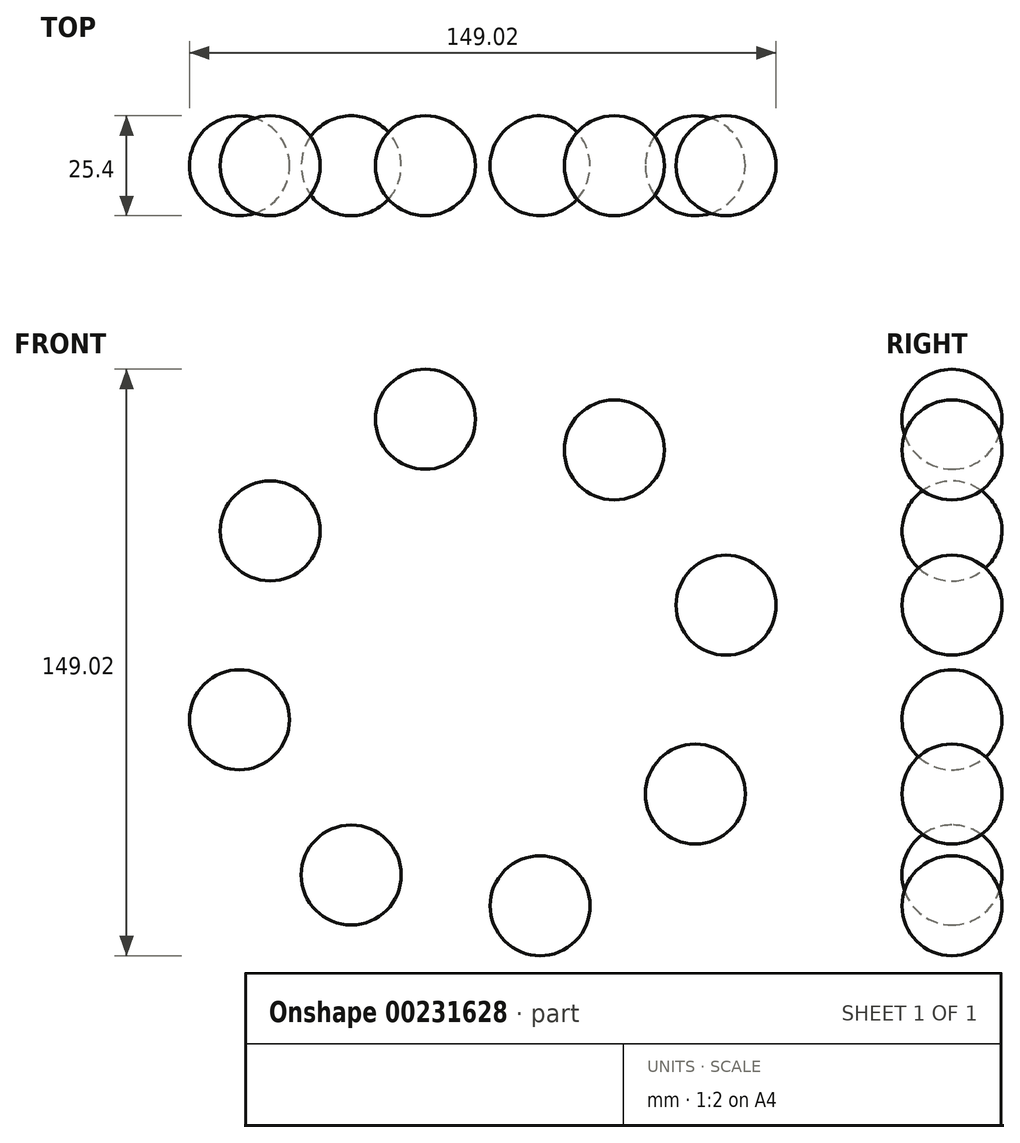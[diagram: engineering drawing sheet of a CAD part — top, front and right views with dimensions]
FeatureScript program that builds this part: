
annotation { "Feature Type Name" : "Feature", "Feature Type Description" : "" }
export const myFeature = defineFeature(function(context is Context, id is Id, definition is map)
    precondition{}
    {
        {
            var Q0;
            Q0=qCreatedBy(makeId("Front.planeOp"),FACE);
            var sketch = newSketch(context, id + "F2", { "sketchPlane" : qUnion([Q0])});
            skCircle(sketch, "E0", {"center": v(0, 0) * mm, "radius": 12.7 * mm});
            skLineSegment(sketch, "E1", {"start": v(0, 28.88) * mm, "end": v(0, -33.86) * mm});
            skCircle(sketch, "E2", {"center": v(33.41, 54) * mm, "radius": 63.5 * mm});
            skPoint(sketch, "E2.second.point", {"position": v(69.32, 106.37) * mm});
            skPoint(sketch, "E2.third.point", {"position": v(83.1, 93.54) * mm});
            skSolve(sketch);
        }
        {
            var Q0;
            {var subQ0=sQuery(id+"F2.wireOp",EDGE,"E1");var subQ1=sQuery(id+"F2.wireOp",EDGE,"E0");var subQ2=makeQuery(id+"F2.imprint","INTERSECT",VERTEX,{"disambiguationData":[OD(1.0)],"derivedFrom":[subQ1,subQ0]});Q0=makeQuery(id+"F2.imprint","IMPRINT",FACE,{"disambiguationData":[TD([[makeQuery(id+"F2.imprint","IMPRINT",EDGE,{"disambiguationData":[TD([[subQ2,1.0]])],"derivedFrom":subQ1}),1.0]])]});}
            var Q1;
            {var subQ0=sQuery(id+"F2.wireOp",EDGE,"E1");var subQ1=sQuery(id+"F2.wireOp",EDGE,"E0");var subQ2=makeQuery(id+"F2.imprint","INTERSECT",VERTEX,{"disambiguationData":[OD(0.0)],"derivedFrom":[subQ1,subQ0]});Q1=makeQuery(id+"F2.imprint","IMPRINT",FACE,{"disambiguationData":[TD([[makeQuery(id+"F2.imprint","IMPRINT",EDGE,{"disambiguationData":[TD([[subQ2,-1.0]])],"derivedFrom":subQ1}),1.0]])]});}
            var Q2;
            Q2=sQuery(id+"F2.wireOp",EDGE,"E1");
            revolve(context, id + "F0", {"entities" : qUnion([Q0, Q1]), "axis" : qUnion([Q2]), "revolveType" : RevolveType.FULL});
        }
        {
            var Q0;
            Q0=makeQuery(id+"F0.opRevolve","SWEPT_BODY",BODY,{"disambiguationData":[OSD([sQuery(id+"F2.wireOp",EDGE,"E0"),sQuery(id+"F2.wireOp",EDGE,"E1")])]});
            var Q1;
            Q1=sQuery(id+"F2.wireOp",EDGE,"E2");
            circularPattern(context, id + "F1", {"entities" : qUnion([Q0]), "axis" : qUnion([Q1]), "angle" : 360 * degree, "instanceCount" : 8, "equalSpace" : true});
        }
    });
